# Revit family: EDFBC12PBC
name_source: partatom
category: Plumbing Fixtures
units: mm (PartAtom-declared; Revit-internal decimal feet)

## family parameters
Always vertical = No
Cut with Voids When Loaded = Yes
OmniClass Number = 23.45.00.00
OmniClass Title = Sanitary, Laundry, and Cleaning Equipment
Part Type = Normal
Room Calculation Point = No
Round Connector Dimension = Use Diameter
Shared = No
Work Plane-Based = Yes

## types (2) — shared parameters
Activation by = Mechanical Top Bubbler Button
Approx. Shipping Weight = 29 lbs.
Assembly Code = D2010810
BUBBLER_MATERIAL = Metal - Steel - Stainless - Chrome
Bubbler Style = Flexi-Guard ® Safety Bubbler
CW Connection = Yes
Chilling Option = Chilling Option
DRAIN_MATERIAL = Metal - Steel - Stainless - Chrome
Default Elevation = 1219 mm
Description = Elkay Countertop Fountain, Non-Filtered Non-Refrigerated Stainless
Drain_Pipe 1 1/2" = 25 mm  [stored 0.082021 ft]
Finish = Stainless Steel
HW Connection = No
Inlet_Pipe = 10 mm  [stored 0.0328084 ft]
Installation Location = Indoor +Outdoor
Manufacturer = Elkay
Mounting Height = 500 mm  [stored 1.64042 ft]
Mounting Type = Recessed Mount
No. of Stations Served = 1
Power = No Electrical Required
SINK_MATERIAL = Metal - Steel - Stainless - Chrome
Vent Connection = No
Version = 1.0.0.0
Waste Connection = Yes

## per-type parameters (varying)
| type | Model |
| DRKR14C | DRKR14C |
| EDFBC12PBC | EDFBC12PBC.rfa |

note: [stored X ft] marks values corroborated as IEEE doubles in the binary element streams (Revit-internal decimal feet)

## geometry (parser evidence)
native form markers: Sweep x17
no freeform markers — native parametric forms only
